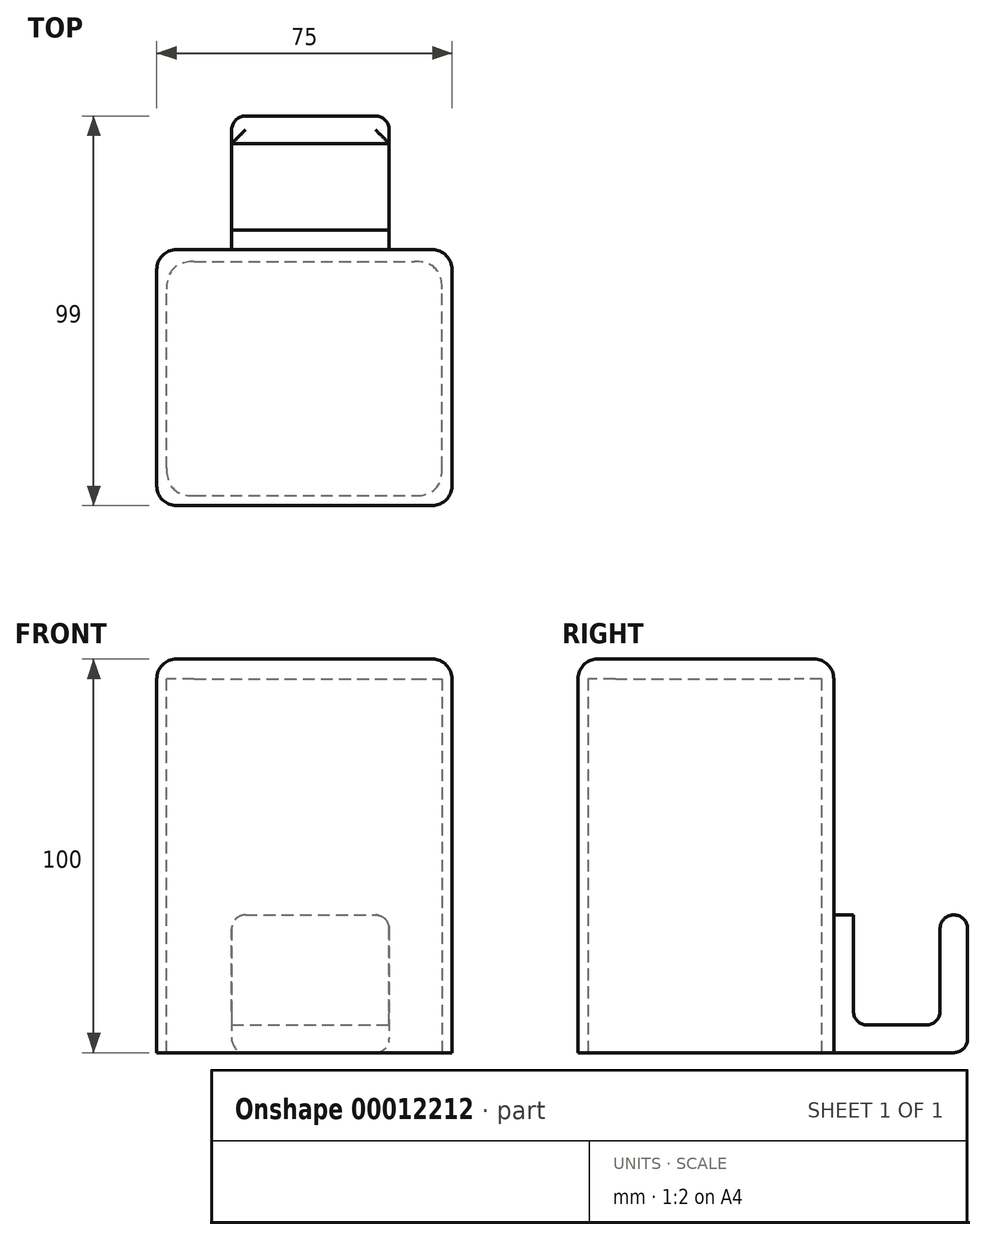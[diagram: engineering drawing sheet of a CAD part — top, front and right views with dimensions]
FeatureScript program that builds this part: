
annotation { "Feature Type Name" : "Feature", "Feature Type Description" : "" }
export const myFeature = defineFeature(function(context is Context, id is Id, definition is map)
    precondition{}
    {
        {
            var Q0;
            Q0=qCreatedBy(makeId("Top.planeOp"),FACE);
            var sketch = newSketch(context, id + "F0", { "sketchPlane" : qUnion([Q0])});
            skLineSegment(sketch, "E0.bottom", {"start": v(-18.45, 34) * mm, "end": v(21.55, 34) * mm});
            skLineSegment(sketch, "E0.top", {"start": v(-18.45, 0) * mm, "end": v(21.55, 0) * mm});
            skLineSegment(sketch, "E0.left", {"start": v(-18.45, 34) * mm, "end": v(-18.45, 0) * mm});
            skLineSegment(sketch, "E0.right", {"start": v(21.55, 34) * mm, "end": v(21.55, 0) * mm});
            skSolve(sketch);
        }
        {
            var Q0;
            Q0=makeQuery(id+"F0.imprint","IMPRINT",FACE,{"disambiguationData":[TD([[makeQuery(id+"F0.imprint","IMPRINT",EDGE,{"derivedFrom":sQuery(id+"F0.wireOp",EDGE,"E0.bottom")}),-1.0]])]});
            extrude(context, id + "F1", {"entities" : qUnion([Q0]), "depth" : 35 * mm});
        }
        {
            var Q0;
            Q0=makeQuery(id+"F1.opExtrude","CAP_FACE",FACE,{"disambiguationData":[OSD([sQuery(id+"F0.wireOp",EDGE,"E0.bottom"),sQuery(id+"F0.wireOp",EDGE,"E0.top"),sQuery(id+"F0.wireOp",EDGE,"E0.left"),sQuery(id+"F0.wireOp",EDGE,"E0.right")])],"isStart":false});
            var sketch = newSketch(context, id + "F2", { "sketchPlane" : qUnion([Q0])});
            skLineSegment(sketch, "E1.bottom", {"start": v(-18.45, 27) * mm, "end": v(21.55, 27) * mm});
            skLineSegment(sketch, "E1.top", {"start": v(-18.45, 5) * mm, "end": v(21.55, 5) * mm});
            skLineSegment(sketch, "E1.left", {"start": v(-18.45, 27) * mm, "end": v(-18.45, 5) * mm});
            skLineSegment(sketch, "E1.right", {"start": v(21.55, 27) * mm, "end": v(21.55, 5) * mm});
            skSolve(sketch);
        }
        {
            var Q0;
            Q0 = qSketchRegion(id + "F2", true);
            extrude(context, id + "F3", {"entities" : qUnion([Q0]), "operationType" : NewBodyOperationType.REMOVE, "oppositeDirection" : true, "depth" : 28 * mm});
        }
        {
            var Q0;
            Q0=makeQuery(id+"F1.opExtrude","CAP_EDGE",EDGE,{"disambiguationData":[OSD([sQuery(id+"F0.wireOp",EDGE,"E0.bottom")])],"isStart":true});
            var Q1;
            Q1=makeQuery(id+"F1.opExtrude","CAP_EDGE",EDGE,{"disambiguationData":[OSD([sQuery(id+"F0.wireOp",EDGE,"E0.bottom")])],"isStart":false});
            var Q2;
            Q2=makeQuery(id+"F3.boolean.opBoolean","COPY",EDGE,{"derivedFrom":makeQuery(id+"F3.opExtrude","CAP_EDGE",EDGE,{"disambiguationData":[OSD([sQuery(id+"F2.wireOp",EDGE,"E1.bottom")])],"isStart":true})});
            var Q3;
            Q3=makeQuery(id+"F3.boolean.opBoolean","COPY",EDGE,{"derivedFrom":makeQuery(id+"F3.opExtrude","CAP_EDGE",EDGE,{"disambiguationData":[OSD([sQuery(id+"F2.wireOp",EDGE,"E1.bottom")])],"isStart":false})});
            var Q4;
            Q4=makeQuery(id+"F3.boolean.opBoolean","COPY",EDGE,{"derivedFrom":makeQuery(id+"F3.opExtrude","CAP_EDGE",EDGE,{"disambiguationData":[OSD([sQuery(id+"F2.wireOp",EDGE,"E1.top")])],"isStart":false})});
            var Q5;
            Q5=makeQuery(id+"F3.boolean.opBoolean","COPY",EDGE,{"derivedFrom":makeQuery(id+"F3.opExtrude","SWEPT_EDGE",EDGE,{"disambiguationData":[OSD([sQuery(id+"F0.wireOp",EDGE,"E0.left"),sQuery(id+"F2.wireOp",EDGE,"E1.bottom"),sQuery(id+"F2.wireOp",EDGE,"E1.left")])]})});
            var Q6;
            Q6=makeQuery(id+"F1.opExtrude","SWEPT_EDGE",EDGE,{"disambiguationData":[OSD([sQuery(id+"F0.wireOp",EDGE,"E0.bottom"),sQuery(id+"F0.wireOp",EDGE,"E0.left")])]});
            var Q7;
            Q7=makeQuery(id+"F1.opExtrude","SWEPT_EDGE",EDGE,{"disambiguationData":[OSD([sQuery(id+"F0.wireOp",EDGE,"E0.bottom"),sQuery(id+"F0.wireOp",EDGE,"E0.right")])]});
            var Q8;
            Q8=makeQuery(id+"F3.boolean.opBoolean","COPY",EDGE,{"derivedFrom":makeQuery(id+"F3.opExtrude","SWEPT_EDGE",EDGE,{"disambiguationData":[OSD([sQuery(id+"F0.wireOp",EDGE,"E0.right"),sQuery(id+"F2.wireOp",EDGE,"E1.bottom"),sQuery(id+"F2.wireOp",EDGE,"E1.right")])]})});
            var Q9;
            Q9=makeQuery(id+"F3.boolean.opBoolean","COPY",EDGE,{"derivedFrom":makeQuery(id+"F3.opExtrude","CAP_EDGE",EDGE,{"disambiguationData":[OSD([sQuery(id+"F2.wireOp",EDGE,"E1.top")])],"isStart":true})});
            var Q10;
            Q10=makeQuery(id+"F1.opExtrude","CAP_EDGE",EDGE,{"disambiguationData":[OSD([sQuery(id+"F0.wireOp",EDGE,"E0.left")])],"isStart":true});
            var Q11;
            Q11=makeQuery(id+"F1.opExtrude","CAP_EDGE",EDGE,{"disambiguationData":[OSD([sQuery(id+"F0.wireOp",EDGE,"E0.right")])],"isStart":true});
            var Q12;
            {var subQ0=sQuery(id+"F0.wireOp",EDGE,"E0.right");var subQ1=sQuery(id+"F0.wireOp",EDGE,"E0.bottom");Q12=makeQuery(id+"F3.boolean.opBoolean","SPLIT",EDGE,{"disambiguationData":[TD([makeQuery(id+"F1.opExtrude","SWEPT_FACE",FACE,{"disambiguationData":[OSD([subQ1])]})])],"derivedFrom":makeQuery(id+"F1.opExtrude","CAP_EDGE",EDGE,{"disambiguationData":[OSD([subQ0])],"isStart":false})});}
            var Q13;
            {var subQ0=sQuery(id+"F0.wireOp",EDGE,"E0.left");var subQ1=sQuery(id+"F0.wireOp",EDGE,"E0.bottom");Q13=makeQuery(id+"F3.boolean.opBoolean","SPLIT",EDGE,{"disambiguationData":[TD([makeQuery(id+"F1.opExtrude","SWEPT_FACE",FACE,{"disambiguationData":[OSD([subQ1])]})])],"derivedFrom":makeQuery(id+"F1.opExtrude","CAP_EDGE",EDGE,{"disambiguationData":[OSD([subQ0])],"isStart":false})});}
            var Q14;
            {var subQ0=sQuery(id+"F0.wireOp",EDGE,"E0.left");var subQ1=sQuery(id+"F0.wireOp",EDGE,"E0.top");Q14=makeQuery(id+"F3.boolean.opBoolean","SPLIT",EDGE,{"disambiguationData":[TD([makeQuery(id+"F1.opExtrude","SWEPT_FACE",FACE,{"disambiguationData":[OSD([subQ1])]})])],"derivedFrom":makeQuery(id+"F1.opExtrude","CAP_EDGE",EDGE,{"disambiguationData":[OSD([subQ0])],"isStart":false})});}
            var Q15;
            {var subQ0=sQuery(id+"F0.wireOp",EDGE,"E0.right");var subQ1=sQuery(id+"F0.wireOp",EDGE,"E0.top");Q15=makeQuery(id+"F3.boolean.opBoolean","SPLIT",EDGE,{"disambiguationData":[TD([makeQuery(id+"F1.opExtrude","SWEPT_FACE",FACE,{"disambiguationData":[OSD([subQ1])]})])],"derivedFrom":makeQuery(id+"F1.opExtrude","CAP_EDGE",EDGE,{"disambiguationData":[OSD([subQ0])],"isStart":false})});}
            fillet(context, id + "F4", {"entities" : qUnion([Q0, Q1, Q2, Q3, Q4, Q5, Q6, Q7, Q8, Q9, Q10, Q11, Q12, Q13, Q14, Q15]), "radius" : 3.5 * mm, "tangentPropagation" : true, "allowEdgeOverflow" : false});
        }
        {
            var Q0;
            Q0=qCreatedBy(makeId("Top.planeOp"),FACE);
            var sketch = newSketch(context, id + "F5", { "sketchPlane" : qUnion([Q0])});
            skLineSegment(sketch, "E2.bottom", {"start": v(-37.5, 0) * mm, "end": v(37.5, 0) * mm});
            skLineSegment(sketch, "E2.top", {"start": v(-37.5, -65) * mm, "end": v(37.5, -65) * mm});
            skLineSegment(sketch, "E2.left", {"start": v(-37.5, 0) * mm, "end": v(-37.5, -65) * mm});
            skLineSegment(sketch, "E2.right", {"start": v(37.5, 0) * mm, "end": v(37.5, -65) * mm});
            skSolve(sketch);
        }
        {
            var Q0;
            Q0 = qSketchRegion(id + "F5", true);
            extrude(context, id + "F6", {"entities" : qUnion([Q0]), "operationType" : NewBodyOperationType.ADD, "depth" : 100 * mm});
        }
        {
            var Q0;
            Q0=makeQuery(id+"F6.boolean.opBoolean","MERGE",FACE,{"derivedFrom":[makeQuery(id+"F1.opExtrude","CAP_FACE",FACE,{"disambiguationData":[OSD([sQuery(id+"F0.wireOp",EDGE,"E0.bottom"),sQuery(id+"F0.wireOp",EDGE,"E0.top"),sQuery(id+"F0.wireOp",EDGE,"E0.left"),sQuery(id+"F0.wireOp",EDGE,"E0.right")])],"isStart":true}),makeQuery(id+"F6.opExtrude","CAP_FACE",FACE,{"disambiguationData":[OSD([sQuery(id+"F5.wireOp",EDGE,"E2.bottom"),sQuery(id+"F5.wireOp",EDGE,"E2.top"),sQuery(id+"F5.wireOp",EDGE,"E2.left"),sQuery(id+"F5.wireOp",EDGE,"E2.right")])],"isStart":true})]});
            var sketch = newSketch(context, id + "F7", { "sketchPlane" : qUnion([Q0])});
            skLineSegment(sketch, "E3.bottom", {"start": v(-35, 62.5) * mm, "end": v(35, 62.5) * mm});
            skLineSegment(sketch, "E3.top", {"start": v(-35, 3) * mm, "end": v(35, 3) * mm});
            skLineSegment(sketch, "E3.left", {"start": v(-35, 62.5) * mm, "end": v(-35, 3) * mm});
            skLineSegment(sketch, "E3.right", {"start": v(35, 62.5) * mm, "end": v(35, 3) * mm});
            skSolve(sketch);
        }
        {
            var Q0;
            Q0=makeQuery(id+"F7.imprint","IMPRINT",FACE,{"disambiguationData":[TD([[makeQuery(id+"F7.imprint","IMPRINT",EDGE,{"derivedFrom":sQuery(id+"F7.wireOp",EDGE,"E3.bottom")}),-1.0]])]});
            extrude(context, id + "F8", {"entities" : qUnion([Q0]), "operationType" : NewBodyOperationType.REMOVE, "oppositeDirection" : true, "depth" : 95 * mm});
        }
        {
            var Q0;
            Q0=makeQuery(id+"F8.boolean.opBoolean","COPY",EDGE,{"derivedFrom":makeQuery(id+"F8.opExtrude","SWEPT_EDGE",EDGE,{"disambiguationData":[OSD([sQuery(id+"F7.wireOp",EDGE,"E3.bottom"),sQuery(id+"F7.wireOp",EDGE,"E3.left")])]})});
            var Q1;
            Q1=makeQuery(id+"F8.boolean.opBoolean","COPY",EDGE,{"derivedFrom":makeQuery(id+"F8.opExtrude","SWEPT_EDGE",EDGE,{"disambiguationData":[OSD([sQuery(id+"F7.wireOp",EDGE,"E3.bottom"),sQuery(id+"F7.wireOp",EDGE,"E3.right")])]})});
            var Q2;
            Q2=makeQuery(id+"F8.boolean.opBoolean","COPY",EDGE,{"derivedFrom":makeQuery(id+"F8.opExtrude","SWEPT_EDGE",EDGE,{"disambiguationData":[OSD([sQuery(id+"F7.wireOp",EDGE,"E3.top"),sQuery(id+"F7.wireOp",EDGE,"E3.left")])]})});
            var Q3;
            Q3=makeQuery(id+"F8.boolean.opBoolean","COPY",EDGE,{"derivedFrom":makeQuery(id+"F8.opExtrude","SWEPT_EDGE",EDGE,{"disambiguationData":[OSD([sQuery(id+"F7.wireOp",EDGE,"E3.top"),sQuery(id+"F7.wireOp",EDGE,"E3.right")])]})});
            fillet(context, id + "F9", {"entities" : qUnion([Q0, Q1, Q2, Q3]), "radius" : 7 * mm, "tangentPropagation" : true, "rho" : 0.5, "crossSection" : FilletCrossSection.CONIC, "allowEdgeOverflow" : false});
        }
        {
            var Q0;
            Q0=makeQuery(id+"F6.opExtrude","SWEPT_EDGE",EDGE,{"disambiguationData":[OSD([sQuery(id+"F5.wireOp",EDGE,"E2.top"),sQuery(id+"F5.wireOp",EDGE,"E2.left")])]});
            var Q1;
            Q1=makeQuery(id+"F6.opExtrude","SWEPT_EDGE",EDGE,{"disambiguationData":[OSD([sQuery(id+"F5.wireOp",EDGE,"E2.bottom"),sQuery(id+"F5.wireOp",EDGE,"E2.left")])]});
            var Q2;
            Q2=makeQuery(id+"F6.opExtrude","SWEPT_EDGE",EDGE,{"disambiguationData":[OSD([sQuery(id+"F5.wireOp",EDGE,"E2.bottom"),sQuery(id+"F5.wireOp",EDGE,"E2.right")])]});
            var Q3;
            Q3=makeQuery(id+"F6.opExtrude","SWEPT_EDGE",EDGE,{"disambiguationData":[OSD([sQuery(id+"F5.wireOp",EDGE,"E2.top"),sQuery(id+"F5.wireOp",EDGE,"E2.right")])]});
            var Q4;
            Q4=makeQuery(id+"F6.opExtrude","CAP_EDGE",EDGE,{"disambiguationData":[OSD([sQuery(id+"F5.wireOp",EDGE,"E2.left")])],"isStart":false});
            var Q5;
            Q5=makeQuery(id+"F6.opExtrude","CAP_EDGE",EDGE,{"disambiguationData":[OSD([sQuery(id+"F5.wireOp",EDGE,"E2.right")])],"isStart":false});
            var Q6;
            Q6=makeQuery(id+"F6.opExtrude","CAP_EDGE",EDGE,{"disambiguationData":[OSD([sQuery(id+"F5.wireOp",EDGE,"E2.top")])],"isStart":false});
            var Q7;
            Q7=makeQuery(id+"F6.opExtrude","CAP_EDGE",EDGE,{"disambiguationData":[OSD([sQuery(id+"F5.wireOp",EDGE,"E2.bottom")])],"isStart":false});
            var Q8;
            Q8=makeQuery(id+"F1.opExtrude","SWEPT_EDGE",EDGE,{"disambiguationData":[OSD([sQuery(id+"F0.wireOp",EDGE,"E0.top"),sQuery(id+"F0.wireOp",EDGE,"E0.left")])]});
            fillet(context, id + "F10", {"entities" : qUnion([Q0, Q1, Q2, Q3, Q4, Q5, Q6, Q7, Q8]), "radius" : 5 * mm, "tangentPropagation" : true, "allowEdgeOverflow" : false});
        }
    });
